# Revit family: Hekatron_Brandmeldetechnik_Sockel 155 UH _DE_23.01
name_source: partatom
category: Brandmelder
revit_build: Autodesk Revit 2018 (Build: 20170223_1515(x64)
units: mm (PartAtom-declared; Revit-internal decimal feet)

## family parameters
Basisbauteil = Fläche
Beim Laden mit Abzugskörper schneiden = Nein
Bemaßung runder Anschluss = Durchmesser verwenden
Beschriftungsausrichtung beibehalten = Ja
Gemeinsam genutzt = Nein
OmniClass-Nummer = 23.85.30.21
OmniClass-Titel = Environmental Detection/Registration
Raumberechnungspunkt = Nein
Teiletyp = Normal

## types (1)
- Sockel 155 UH
    Beschreibung = Funk-Unterputzsockel für Hohldecken
    Durchmesser (mm) = 90.0
    Farbe = weiß
    Hersteller = Hekatron
    Hoehe (mm) = 35.0
    Link zu Ausschreibungstext = https://www.meinhplus.de
    Link zu Produktinformation = https://www.hekatron-brandschutz.de
    Material = Kunststoff
    Modell = Sockel 155 UH
    Nettogewicht (g) = 86.0
    Typenkommentare = Funk-Unterputzsockel für Hohldecken
    UB A&S Artikel Nummer = 31-5000037-01-01
    URL = www.hekatron-brandschutz.de
    Version des BIM Objektes = 23.01
    Vorgabe-Ansicht = 1200 mm

## geometry (parser evidence)
native form markers: Sweep x2
no freeform markers — native parametric forms only
